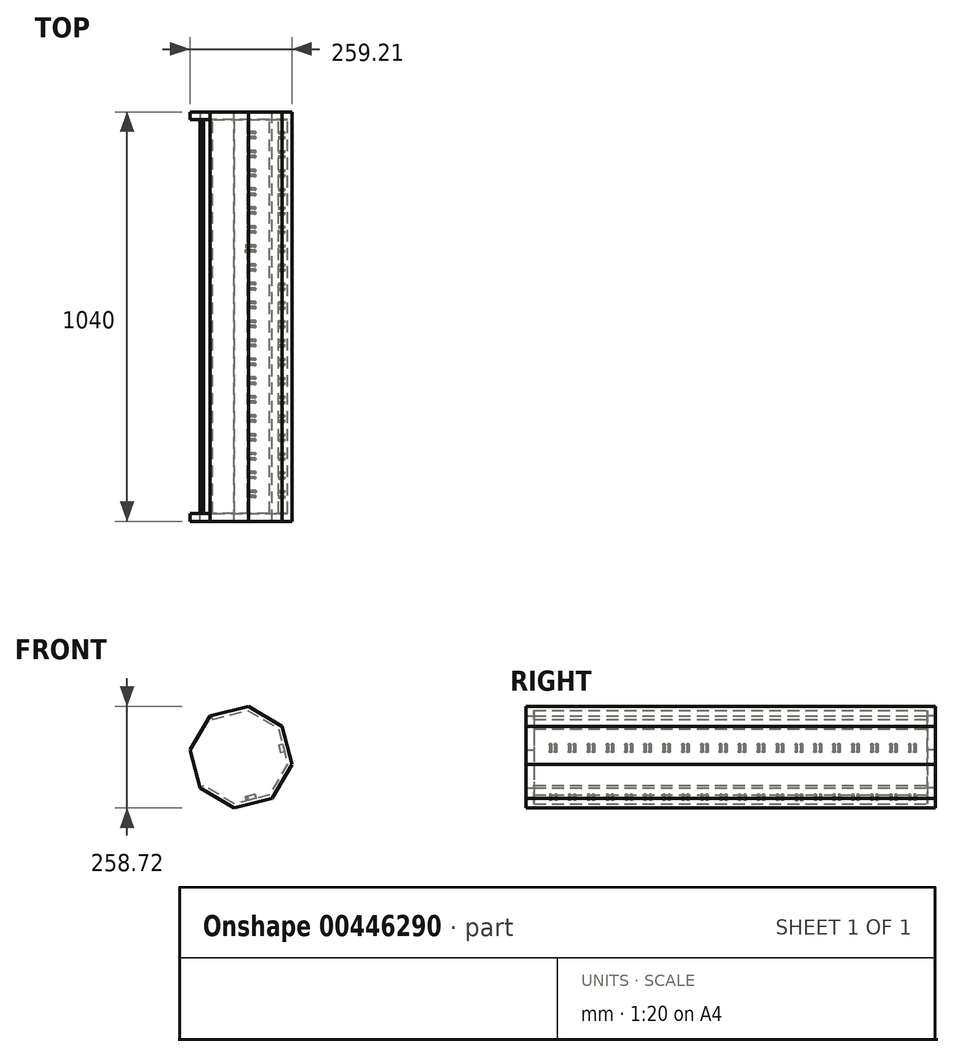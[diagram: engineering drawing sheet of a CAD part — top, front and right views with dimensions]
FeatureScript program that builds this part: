
annotation { "Feature Type Name" : "Feature", "Feature Type Description" : "" }
export const myFeature = defineFeature(function(context is Context, id is Id, definition is map)
    precondition{}
    {
        {
            var Q0;
            Q0=qCreatedBy(makeId("Front.planeOp"),FACE);
            var sketch = newSketch(context, id + "F0", { "sketchPlane" : qUnion([Q0])});
            skCircle(sketch, "E0.cCircle", {"center": v(-103.92, 114.28) * mm, "radius": 120.71 * mm, "construction": true});
            skLineSegment(sketch, "E0.0", {"start": v(25.44, 95.92) * mm, "end": v(-25.44, 9.82) * mm});
            skLineSegment(sketch, "E0.1", {"start": v(-25.44, 9.82) * mm, "end": v(-122.29, -15.08) * mm});
            skLineSegment(sketch, "E0.2", {"start": v(-122.29, -15.08) * mm, "end": v(-208.38, 35.8) * mm});
            skLineSegment(sketch, "E0.5", {"start": v(-182.4, 218.74) * mm, "end": v(-85.56, 243.64) * mm});
            skLineSegment(sketch, "E0.6", {"start": v(-85.56, 243.64) * mm, "end": v(0.53, 192.77) * mm});
            skLineSegment(sketch, "E0.7", {"start": v(0.53, 192.77) * mm, "end": v(25.44, 95.92) * mm});
            skPoint(sketch, "E0.0.midPoint", {"position": v(0, 52.87) * mm});
            skCircle(sketch, "E1.cCircle", {"center": v(-103.92, 114.28) * mm, "radius": 110.71 * mm, "construction": true});
            skLineSegment(sketch, "E1.0", {"start": v(-8.12, 186.26) * mm, "end": v(14.72, 97.44) * mm});
            skLineSegment(sketch, "E1.1", {"start": v(14.72, 97.44) * mm, "end": v(-31.94, 18.48) * mm});
            skLineSegment(sketch, "E1.2", {"start": v(-31.94, 18.48) * mm, "end": v(-120.77, -4.36) * mm});
            skLineSegment(sketch, "E1.3", {"start": v(-120.77, -4.36) * mm, "end": v(-199.73, 42.3) * mm});
            skLineSegment(sketch, "E1.6", {"start": v(-175.9, 210.08) * mm, "end": v(-87.08, 232.92) * mm});
            skLineSegment(sketch, "E1.7", {"start": v(-87.08, 232.92) * mm, "end": v(-8.12, 186.26) * mm});
            skPoint(sketch, "E1.0.midPoint", {"position": v(3.3, 141.85) * mm});
            skLineSegment(sketch, "E2", {"start": v(-182.4, 218.74) * mm, "end": v(-175.9, 210.08) * mm});
            skLineSegment(sketch, "E3", {"start": v(-208.38, 35.8) * mm, "end": v(-199.73, 42.3) * mm});
            skSolve(sketch);
        }
        {
            var Q0;
            Q0 = qSketchRegion(id + "F0", true);
            extrude(context, id + "F1", {"entities" : qUnion([Q0]), "depth" : 1000 * mm});
        }
        {
            var Q0;
            Q0=makeQuery(id+"F1.opExtrude","CAP_FACE",FACE,{"disambiguationData":[OSD([sQuery(id+"F0.wireOp",EDGE,"E0.0"),sQuery(id+"F0.wireOp",EDGE,"E0.1"),sQuery(id+"F0.wireOp",EDGE,"E0.2"),sQuery(id+"F0.wireOp",EDGE,"E0.5"),sQuery(id+"F0.wireOp",EDGE,"E0.6"),sQuery(id+"F0.wireOp",EDGE,"E0.7"),sQuery(id+"F0.wireOp",EDGE,"E1.0"),sQuery(id+"F0.wireOp",EDGE,"E1.1"),sQuery(id+"F0.wireOp",EDGE,"E1.2"),sQuery(id+"F0.wireOp",EDGE,"E1.3"),sQuery(id+"F0.wireOp",EDGE,"E1.6"),sQuery(id+"F0.wireOp",EDGE,"E1.7"),sQuery(id+"F0.wireOp",EDGE,"E2"),sQuery(id+"F0.wireOp",EDGE,"E3")])],"isStart":false});
            var sketch = newSketch(context, id + "F2", { "sketchPlane" : qUnion([Q0])});
            skLineSegment(sketch, "E4", {"start": v(-182.4, 218.74) * mm, "end": v(-233.28, 132.65) * mm});
            skLineSegment(sketch, "E5", {"start": v(-233.28, 132.65) * mm, "end": v(-208.38, 35.8) * mm});
            skLineSegment(sketch, "E6", {"start": v(-208.38, 35.8) * mm, "end": v(-122.29, -15.08) * mm});
            skLineSegment(sketch, "E7", {"start": v(-122.29, -15.08) * mm, "end": v(-25.44, 9.82) * mm});
            skLineSegment(sketch, "E8", {"start": v(-25.44, 9.82) * mm, "end": v(25.44, 95.92) * mm});
            skLineSegment(sketch, "E9", {"start": v(25.44, 95.92) * mm, "end": v(0.53, 192.77) * mm});
            skLineSegment(sketch, "E10", {"start": v(0.53, 192.77) * mm, "end": v(-85.56, 243.64) * mm});
            skLineSegment(sketch, "E11", {"start": v(-85.56, 243.64) * mm, "end": v(-182.4, 218.74) * mm});
            skSolve(sketch);
        }
        {
            var Q0;
            Q0 = qSketchRegion(id + "F2", true);
            extrude(context, id + "F3", {"entities" : qUnion([Q0]), "operationType" : NewBodyOperationType.ADD, "depth" : 20 * mm});
        }
        {
            var Q0;
            Q0=makeQuery(id+"F1.opExtrude","CAP_FACE",FACE,{"disambiguationData":[OSD([sQuery(id+"F0.wireOp",EDGE,"E0.0"),sQuery(id+"F0.wireOp",EDGE,"E0.1"),sQuery(id+"F0.wireOp",EDGE,"E0.2"),sQuery(id+"F0.wireOp",EDGE,"E0.5"),sQuery(id+"F0.wireOp",EDGE,"E0.6"),sQuery(id+"F0.wireOp",EDGE,"E0.7"),sQuery(id+"F0.wireOp",EDGE,"E1.0"),sQuery(id+"F0.wireOp",EDGE,"E1.1"),sQuery(id+"F0.wireOp",EDGE,"E1.2"),sQuery(id+"F0.wireOp",EDGE,"E1.3"),sQuery(id+"F0.wireOp",EDGE,"E1.6"),sQuery(id+"F0.wireOp",EDGE,"E1.7"),sQuery(id+"F0.wireOp",EDGE,"E2"),sQuery(id+"F0.wireOp",EDGE,"E3")])],"isStart":true});
            var sketch = newSketch(context, id + "F4", { "sketchPlane" : qUnion([Q0])});
            skLineSegment(sketch, "E12", {"start": v(182.4, 218.74) * mm, "end": v(85.56, 243.64) * mm});
            skLineSegment(sketch, "E13", {"start": v(85.56, 243.64) * mm, "end": v(-0.53, 192.77) * mm});
            skLineSegment(sketch, "E14", {"start": v(-0.53, 192.77) * mm, "end": v(-25.44, 95.92) * mm});
            skLineSegment(sketch, "E15", {"start": v(-25.44, 95.92) * mm, "end": v(25.44, 9.82) * mm});
            skLineSegment(sketch, "E16", {"start": v(25.44, 9.82) * mm, "end": v(122.29, -15.08) * mm});
            skLineSegment(sketch, "E17", {"start": v(122.29, -15.08) * mm, "end": v(208.38, 35.8) * mm});
            skLineSegment(sketch, "E18", {"start": v(208.38, 35.8) * mm, "end": v(233.77, 133.25) * mm});
            skLineSegment(sketch, "E19", {"start": v(233.77, 133.25) * mm, "end": v(182.4, 218.74) * mm});
            skSolve(sketch);
        }
        {
            var Q0;
            Q0 = qSketchRegion(id + "F4", true);
            extrude(context, id + "F5", {"entities" : qUnion([Q0]), "operationType" : NewBodyOperationType.ADD, "depth" : 20 * mm});
        }
        {
            var Q0;
            Q0=makeQuery(id+"F1.opExtrude","SWEPT_FACE",FACE,{"disambiguationData":[OSD([sQuery(id+"F0.wireOp",EDGE,"E1.0")])]});
            var sketch = newSketch(context, id + "F6", { "sketchPlane" : qUnion([Q0])});
            skLineSegment(sketch, "E20.bottom", {"start": v(30, 143.31) * mm, "end": v(35, 143.31) * mm});
            skLineSegment(sketch, "E20.top", {"start": v(30, 123.31) * mm, "end": v(35, 123.31) * mm});
            skLineSegment(sketch, "E20.left", {"start": v(30, 143.31) * mm, "end": v(30, 123.31) * mm});
            skLineSegment(sketch, "E20.right", {"start": v(35, 143.31) * mm, "end": v(35, 123.31) * mm});
            skLineSegment(sketch, "E21.bottom", {"start": v(43, 143.33) * mm, "end": v(48, 143.33) * mm});
            skLineSegment(sketch, "E21.top", {"start": v(43, 123.33) * mm, "end": v(48, 123.33) * mm});
            skLineSegment(sketch, "E21.left", {"start": v(43, 143.33) * mm, "end": v(43, 123.33) * mm});
            skLineSegment(sketch, "E21.right", {"start": v(48, 143.33) * mm, "end": v(48, 123.33) * mm});
            skLineSegment(sketch, "E22.bottom", {"start": v(78, 143.31) * mm, "end": v(83.3, 143.31) * mm});
            skLineSegment(sketch, "E22.top", {"start": v(78, 123.31) * mm, "end": v(83.3, 123.31) * mm});
            skLineSegment(sketch, "E22.left", {"start": v(78, 143.31) * mm, "end": v(78, 123.31) * mm});
            skLineSegment(sketch, "E22.right", {"start": v(83.3, 143.31) * mm, "end": v(83.3, 123.31) * mm});
            skLineSegment(sketch, "E23.bottom", {"start": v(91.3, 143.31) * mm, "end": v(96.3, 143.31) * mm});
            skLineSegment(sketch, "E23.top", {"start": v(91.3, 123.09) * mm, "end": v(96.3, 123.09) * mm});
            skLineSegment(sketch, "E23.left", {"start": v(91.3, 143.31) * mm, "end": v(91.3, 123.09) * mm});
            skLineSegment(sketch, "E23.right", {"start": v(96.3, 143.31) * mm, "end": v(96.3, 123.09) * mm});
            skLineSegment(sketch, "E24.bottom", {"start": v(126.3, 143.31) * mm, "end": v(131.3, 143.31) * mm});
            skLineSegment(sketch, "E24.top", {"start": v(126.3, 123.31) * mm, "end": v(131.3, 123.31) * mm});
            skLineSegment(sketch, "E24.left", {"start": v(126.3, 143.31) * mm, "end": v(126.3, 123.31) * mm});
            skLineSegment(sketch, "E24.right", {"start": v(131.3, 143.31) * mm, "end": v(131.3, 123.31) * mm});
            skLineSegment(sketch, "E25.bottom", {"start": v(139.3, 143.31) * mm, "end": v(144.3, 143.31) * mm});
            skLineSegment(sketch, "E25.top", {"start": v(139.3, 123.54) * mm, "end": v(144.3, 123.54) * mm});
            skLineSegment(sketch, "E25.left", {"start": v(139.3, 143.31) * mm, "end": v(139.3, 123.54) * mm});
            skLineSegment(sketch, "E25.right", {"start": v(144.3, 143.31) * mm, "end": v(144.3, 123.54) * mm});
            skLineSegment(sketch, "E26.bottom", {"start": v(174.3, 143.31) * mm, "end": v(179.3, 143.31) * mm});
            skLineSegment(sketch, "E26.top", {"start": v(174.3, 123.31) * mm, "end": v(179.3, 123.31) * mm});
            skLineSegment(sketch, "E26.left", {"start": v(174.3, 143.31) * mm, "end": v(174.3, 123.31) * mm});
            skLineSegment(sketch, "E26.right", {"start": v(179.3, 143.31) * mm, "end": v(179.3, 123.31) * mm});
            skLineSegment(sketch, "E27.bottom", {"start": v(187.3, 143.31) * mm, "end": v(192.3, 143.31) * mm});
            skLineSegment(sketch, "E27.top", {"start": v(187.3, 123.31) * mm, "end": v(192.3, 123.31) * mm});
            skLineSegment(sketch, "E27.left", {"start": v(187.3, 143.31) * mm, "end": v(187.3, 123.31) * mm});
            skLineSegment(sketch, "E27.right", {"start": v(192.3, 143.31) * mm, "end": v(192.3, 123.31) * mm});
            skLineSegment(sketch, "E28.bottom", {"start": v(222.3, 143.31) * mm, "end": v(227.3, 143.31) * mm});
            skLineSegment(sketch, "E28.top", {"start": v(222.3, 123.31) * mm, "end": v(227.3, 123.31) * mm});
            skLineSegment(sketch, "E28.left", {"start": v(222.3, 143.31) * mm, "end": v(222.3, 123.31) * mm});
            skLineSegment(sketch, "E28.right", {"start": v(227.3, 143.31) * mm, "end": v(227.3, 123.31) * mm});
            skLineSegment(sketch, "E29.bottom", {"start": v(235.3, 143.31) * mm, "end": v(240.3, 143.31) * mm});
            skLineSegment(sketch, "E29.top", {"start": v(235.3, 123.31) * mm, "end": v(240.3, 123.31) * mm});
            skLineSegment(sketch, "E29.left", {"start": v(235.3, 143.31) * mm, "end": v(235.3, 123.31) * mm});
            skLineSegment(sketch, "E29.right", {"start": v(240.3, 143.31) * mm, "end": v(240.3, 123.31) * mm});
            skLineSegment(sketch, "E30.bottom", {"start": v(270.3, 143.31) * mm, "end": v(275.3, 143.31) * mm});
            skLineSegment(sketch, "E30.top", {"start": v(270.3, 123.31) * mm, "end": v(275.3, 123.31) * mm});
            skLineSegment(sketch, "E30.left", {"start": v(270.3, 143.31) * mm, "end": v(270.3, 123.31) * mm});
            skLineSegment(sketch, "E30.right", {"start": v(275.3, 143.31) * mm, "end": v(275.3, 123.31) * mm});
            skLineSegment(sketch, "E31.bottom", {"start": v(283.3, 143.31) * mm, "end": v(288.3, 143.31) * mm});
            skLineSegment(sketch, "E31.top", {"start": v(283.3, 123.31) * mm, "end": v(288.3, 123.31) * mm});
            skLineSegment(sketch, "E31.left", {"start": v(283.3, 143.31) * mm, "end": v(283.3, 123.31) * mm});
            skLineSegment(sketch, "E31.right", {"start": v(288.3, 143.31) * mm, "end": v(288.3, 123.31) * mm});
            skLineSegment(sketch, "E32.bottom", {"start": v(318.3, 143.31) * mm, "end": v(323.3, 143.31) * mm});
            skLineSegment(sketch, "E32.top", {"start": v(318.3, 123.31) * mm, "end": v(323.3, 123.31) * mm});
            skLineSegment(sketch, "E32.left", {"start": v(318.3, 143.31) * mm, "end": v(318.3, 123.31) * mm});
            skLineSegment(sketch, "E32.right", {"start": v(323.3, 143.31) * mm, "end": v(323.3, 123.31) * mm});
            skLineSegment(sketch, "E33.bottom", {"start": v(331.3, 143.31) * mm, "end": v(336.3, 143.31) * mm});
            skLineSegment(sketch, "E33.top", {"start": v(331.3, 123.31) * mm, "end": v(336.3, 123.31) * mm});
            skLineSegment(sketch, "E33.left", {"start": v(331.3, 143.31) * mm, "end": v(331.3, 123.31) * mm});
            skLineSegment(sketch, "E33.right", {"start": v(336.3, 143.31) * mm, "end": v(336.3, 123.31) * mm});
            skLineSegment(sketch, "E34.bottom", {"start": v(366.3, 143.31) * mm, "end": v(371.3, 143.31) * mm});
            skLineSegment(sketch, "E34.top", {"start": v(366.3, 123.31) * mm, "end": v(371.3, 123.31) * mm});
            skLineSegment(sketch, "E34.left", {"start": v(366.3, 143.31) * mm, "end": v(366.3, 123.31) * mm});
            skLineSegment(sketch, "E34.right", {"start": v(371.3, 143.31) * mm, "end": v(371.3, 123.31) * mm});
            skPoint(sketch, "E35.firstSnap0", {"position": v(368.8, 143.31) * mm});
            skLineSegment(sketch, "E35.bottom", {"start": v(379.3, 143.31) * mm, "end": v(384.3, 143.31) * mm});
            skLineSegment(sketch, "E35.top", {"start": v(379.3, 123.31) * mm, "end": v(384.3, 123.31) * mm});
            skLineSegment(sketch, "E35.left", {"start": v(379.3, 143.31) * mm, "end": v(379.3, 123.31) * mm});
            skLineSegment(sketch, "E35.right", {"start": v(384.3, 143.31) * mm, "end": v(384.3, 123.31) * mm});
            skLineSegment(sketch, "E36.bottom", {"start": v(414.3, 143.31) * mm, "end": v(419.3, 143.31) * mm});
            skLineSegment(sketch, "E36.top", {"start": v(414.3, 123.31) * mm, "end": v(419.3, 123.31) * mm});
            skLineSegment(sketch, "E36.left", {"start": v(414.3, 143.31) * mm, "end": v(414.3, 123.31) * mm});
            skLineSegment(sketch, "E36.right", {"start": v(419.3, 143.31) * mm, "end": v(419.3, 123.31) * mm});
            skPoint(sketch, "E37.firstSnap0", {"position": v(416.8, 143.31) * mm});
            skLineSegment(sketch, "E37.bottom", {"start": v(427.3, 143.31) * mm, "end": v(432.3, 143.31) * mm});
            skLineSegment(sketch, "E37.top", {"start": v(427.3, 123.31) * mm, "end": v(432.3, 123.31) * mm});
            skLineSegment(sketch, "E37.left", {"start": v(427.3, 143.31) * mm, "end": v(427.3, 123.31) * mm});
            skLineSegment(sketch, "E37.right", {"start": v(432.3, 143.31) * mm, "end": v(432.3, 123.31) * mm});
            skLineSegment(sketch, "E38.bottom", {"start": v(462.3, 143.31) * mm, "end": v(467.3, 143.31) * mm});
            skLineSegment(sketch, "E38.top", {"start": v(462.3, 123.31) * mm, "end": v(467.3, 123.31) * mm});
            skLineSegment(sketch, "E38.left", {"start": v(462.3, 143.31) * mm, "end": v(462.3, 123.31) * mm});
            skLineSegment(sketch, "E38.right", {"start": v(467.3, 143.31) * mm, "end": v(467.3, 123.31) * mm});
            skLineSegment(sketch, "E39.bottom", {"start": v(475.3, 143.31) * mm, "end": v(480.3, 143.31) * mm});
            skLineSegment(sketch, "E39.top", {"start": v(475.3, 123.31) * mm, "end": v(480.3, 123.31) * mm});
            skLineSegment(sketch, "E39.left", {"start": v(475.3, 143.31) * mm, "end": v(475.3, 123.31) * mm});
            skLineSegment(sketch, "E39.right", {"start": v(480.3, 143.31) * mm, "end": v(480.3, 123.31) * mm});
            skLineSegment(sketch, "E40.bottom", {"start": v(510.3, 143.31) * mm, "end": v(515.3, 143.31) * mm});
            skLineSegment(sketch, "E40.top", {"start": v(510.3, 123.31) * mm, "end": v(515.3, 123.31) * mm});
            skLineSegment(sketch, "E40.left", {"start": v(510.3, 143.31) * mm, "end": v(510.3, 123.31) * mm});
            skLineSegment(sketch, "E40.right", {"start": v(515.3, 143.31) * mm, "end": v(515.3, 123.31) * mm});
            skPoint(sketch, "E41.firstSnap0", {"position": v(512.8, 143.31) * mm});
            skLineSegment(sketch, "E41.bottom", {"start": v(523.3, 143.31) * mm, "end": v(528.3, 143.31) * mm});
            skLineSegment(sketch, "E41.top", {"start": v(523.3, 123.31) * mm, "end": v(528.3, 123.31) * mm});
            skLineSegment(sketch, "E41.left", {"start": v(523.3, 143.31) * mm, "end": v(523.3, 123.31) * mm});
            skLineSegment(sketch, "E41.right", {"start": v(528.3, 143.31) * mm, "end": v(528.3, 123.31) * mm});
            skPoint(sketch, "E42.firstSnap0", {"position": v(525.8, 143.31) * mm});
            skLineSegment(sketch, "E42.bottom", {"start": v(558.3, 143.31) * mm, "end": v(563.3, 143.31) * mm});
            skLineSegment(sketch, "E42.top", {"start": v(558.3, 123.31) * mm, "end": v(563.3, 123.31) * mm});
            skLineSegment(sketch, "E42.left", {"start": v(558.3, 143.31) * mm, "end": v(558.3, 123.31) * mm});
            skLineSegment(sketch, "E42.right", {"start": v(563.3, 143.31) * mm, "end": v(563.3, 123.31) * mm});
            skPoint(sketch, "E43.firstSnap0", {"position": v(560.8, 143.31) * mm});
            skLineSegment(sketch, "E43.bottom", {"start": v(571.3, 143.31) * mm, "end": v(576.3, 143.31) * mm});
            skLineSegment(sketch, "E43.top", {"start": v(571.3, 123.31) * mm, "end": v(576.3, 123.31) * mm});
            skLineSegment(sketch, "E43.left", {"start": v(571.3, 143.31) * mm, "end": v(571.3, 123.31) * mm});
            skLineSegment(sketch, "E43.right", {"start": v(576.3, 143.31) * mm, "end": v(576.3, 123.31) * mm});
            skPoint(sketch, "E44.firstSnap0", {"position": v(573.8, 143.31) * mm});
            skLineSegment(sketch, "E44.bottom", {"start": v(606.3, 143.31) * mm, "end": v(611.3, 143.31) * mm});
            skLineSegment(sketch, "E44.top", {"start": v(606.3, 123.31) * mm, "end": v(611.3, 123.31) * mm});
            skLineSegment(sketch, "E44.left", {"start": v(606.3, 143.31) * mm, "end": v(606.3, 123.31) * mm});
            skLineSegment(sketch, "E44.right", {"start": v(611.3, 143.31) * mm, "end": v(611.3, 123.31) * mm});
            skPoint(sketch, "E45.firstSnap0", {"position": v(608.8, 143.31) * mm});
            skLineSegment(sketch, "E45.bottom", {"start": v(619.3, 143.31) * mm, "end": v(624.3, 143.31) * mm});
            skLineSegment(sketch, "E45.top", {"start": v(619.3, 123.31) * mm, "end": v(624.3, 123.31) * mm});
            skLineSegment(sketch, "E45.left", {"start": v(619.3, 143.31) * mm, "end": v(619.3, 123.31) * mm});
            skLineSegment(sketch, "E45.right", {"start": v(624.3, 143.31) * mm, "end": v(624.3, 123.31) * mm});
            skLineSegment(sketch, "E46.bottom", {"start": v(654.3, 143.31) * mm, "end": v(659.3, 143.31) * mm});
            skLineSegment(sketch, "E46.top", {"start": v(654.3, 123.31) * mm, "end": v(659.3, 123.31) * mm});
            skLineSegment(sketch, "E46.left", {"start": v(654.3, 143.31) * mm, "end": v(654.3, 123.31) * mm});
            skLineSegment(sketch, "E46.right", {"start": v(659.3, 143.31) * mm, "end": v(659.3, 123.31) * mm});
            skLineSegment(sketch, "E47.bottom", {"start": v(667.3, 143.31) * mm, "end": v(672.3, 143.31) * mm});
            skLineSegment(sketch, "E47.top", {"start": v(667.3, 123.31) * mm, "end": v(672.3, 123.31) * mm});
            skLineSegment(sketch, "E47.left", {"start": v(667.3, 143.31) * mm, "end": v(667.3, 123.31) * mm});
            skLineSegment(sketch, "E47.right", {"start": v(672.3, 143.31) * mm, "end": v(672.3, 123.31) * mm});
            skLineSegment(sketch, "E48.bottom", {"start": v(702.3, 143.31) * mm, "end": v(707.3, 143.31) * mm});
            skLineSegment(sketch, "E48.top", {"start": v(702.3, 123.31) * mm, "end": v(707.3, 123.31) * mm});
            skLineSegment(sketch, "E48.left", {"start": v(702.3, 143.31) * mm, "end": v(702.3, 123.31) * mm});
            skLineSegment(sketch, "E48.right", {"start": v(707.3, 143.31) * mm, "end": v(707.3, 123.31) * mm});
            skPoint(sketch, "E49.firstSnap0", {"position": v(704.8, 143.31) * mm});
            skLineSegment(sketch, "E49.bottom", {"start": v(715.3, 143.31) * mm, "end": v(720.3, 143.31) * mm});
            skLineSegment(sketch, "E49.top", {"start": v(715.3, 123.31) * mm, "end": v(720.3, 123.31) * mm});
            skLineSegment(sketch, "E49.left", {"start": v(715.3, 143.31) * mm, "end": v(715.3, 123.31) * mm});
            skLineSegment(sketch, "E49.right", {"start": v(720.3, 143.31) * mm, "end": v(720.3, 123.31) * mm});
            skPoint(sketch, "E50.firstSnap0", {"position": v(717.8, 143.31) * mm});
            skLineSegment(sketch, "E50.bottom", {"start": v(750.3, 143.31) * mm, "end": v(755.3, 143.31) * mm});
            skLineSegment(sketch, "E50.top", {"start": v(750.3, 123.31) * mm, "end": v(755.3, 123.31) * mm});
            skLineSegment(sketch, "E50.left", {"start": v(750.3, 143.31) * mm, "end": v(750.3, 123.31) * mm});
            skLineSegment(sketch, "E50.right", {"start": v(755.3, 143.31) * mm, "end": v(755.3, 123.31) * mm});
            skPoint(sketch, "E51.firstSnap0", {"position": v(752.8, 143.31) * mm});
            skLineSegment(sketch, "E51.bottom", {"start": v(763.3, 143.31) * mm, "end": v(768.3, 143.31) * mm});
            skLineSegment(sketch, "E51.top", {"start": v(763.3, 123.31) * mm, "end": v(768.3, 123.31) * mm});
            skLineSegment(sketch, "E51.left", {"start": v(763.3, 143.31) * mm, "end": v(763.3, 123.31) * mm});
            skLineSegment(sketch, "E51.right", {"start": v(768.3, 143.31) * mm, "end": v(768.3, 123.31) * mm});
            skPoint(sketch, "E52.firstSnap0", {"position": v(765.8, 143.31) * mm});
            skLineSegment(sketch, "E52.bottom", {"start": v(798.3, 143.31) * mm, "end": v(803.3, 143.31) * mm});
            skLineSegment(sketch, "E52.top", {"start": v(798.3, 123.31) * mm, "end": v(803.3, 123.31) * mm});
            skLineSegment(sketch, "E52.left", {"start": v(798.3, 143.31) * mm, "end": v(798.3, 123.31) * mm});
            skLineSegment(sketch, "E52.right", {"start": v(803.3, 143.31) * mm, "end": v(803.3, 123.31) * mm});
            skPoint(sketch, "E53.firstSnap0", {"position": v(800.8, 143.31) * mm});
            skLineSegment(sketch, "E53.bottom", {"start": v(811.3, 143.31) * mm, "end": v(816.3, 143.31) * mm});
            skLineSegment(sketch, "E53.top", {"start": v(811.3, 123.31) * mm, "end": v(816.3, 123.31) * mm});
            skLineSegment(sketch, "E53.left", {"start": v(811.3, 143.31) * mm, "end": v(811.3, 123.31) * mm});
            skLineSegment(sketch, "E53.right", {"start": v(816.3, 143.31) * mm, "end": v(816.3, 123.31) * mm});
            skLineSegment(sketch, "E54.bottom", {"start": v(846.3, 143.31) * mm, "end": v(851.3, 143.31) * mm});
            skLineSegment(sketch, "E54.top", {"start": v(846.3, 123.31) * mm, "end": v(851.3, 123.31) * mm});
            skLineSegment(sketch, "E54.left", {"start": v(846.3, 143.31) * mm, "end": v(846.3, 123.31) * mm});
            skLineSegment(sketch, "E54.right", {"start": v(851.3, 143.31) * mm, "end": v(851.3, 123.31) * mm});
            skLineSegment(sketch, "E55.bottom", {"start": v(859.3, 143.31) * mm, "end": v(864.3, 143.31) * mm});
            skLineSegment(sketch, "E55.top", {"start": v(859.3, 123.31) * mm, "end": v(864.3, 123.31) * mm});
            skLineSegment(sketch, "E55.left", {"start": v(859.3, 143.31) * mm, "end": v(859.3, 123.31) * mm});
            skLineSegment(sketch, "E55.right", {"start": v(864.3, 143.31) * mm, "end": v(864.3, 123.31) * mm});
            skLineSegment(sketch, "E56.bottom", {"start": v(894.3, 143.31) * mm, "end": v(899.3, 143.31) * mm});
            skLineSegment(sketch, "E56.top", {"start": v(894.3, 123.3) * mm, "end": v(899.3, 123.3) * mm});
            skLineSegment(sketch, "E56.left", {"start": v(894.3, 143.31) * mm, "end": v(894.3, 123.3) * mm});
            skLineSegment(sketch, "E56.right", {"start": v(899.3, 143.31) * mm, "end": v(899.3, 123.3) * mm});
            skLineSegment(sketch, "E57.bottom", {"start": v(907.3, 143.31) * mm, "end": v(912.3, 143.31) * mm});
            skLineSegment(sketch, "E57.top", {"start": v(907.3, 123.31) * mm, "end": v(912.3, 123.31) * mm});
            skLineSegment(sketch, "E57.left", {"start": v(907.3, 143.31) * mm, "end": v(907.3, 123.31) * mm});
            skLineSegment(sketch, "E57.right", {"start": v(912.3, 143.31) * mm, "end": v(912.3, 123.31) * mm});
            skLineSegment(sketch, "E58.bottom", {"start": v(942.3, 143.31) * mm, "end": v(947.3, 143.31) * mm});
            skLineSegment(sketch, "E58.top", {"start": v(942.3, 123.31) * mm, "end": v(947.3, 123.31) * mm});
            skLineSegment(sketch, "E58.left", {"start": v(942.3, 143.31) * mm, "end": v(942.3, 123.31) * mm});
            skLineSegment(sketch, "E58.right", {"start": v(947.3, 143.31) * mm, "end": v(947.3, 123.31) * mm});
            skLineSegment(sketch, "E59.bottom", {"start": v(955.3, 143.31) * mm, "end": v(960.3, 143.31) * mm});
            skLineSegment(sketch, "E59.top", {"start": v(955.3, 123.31) * mm, "end": v(960.3, 123.31) * mm});
            skLineSegment(sketch, "E59.left", {"start": v(955.3, 143.31) * mm, "end": v(955.3, 123.31) * mm});
            skLineSegment(sketch, "E59.right", {"start": v(960.3, 143.31) * mm, "end": v(960.3, 123.31) * mm});
            skSolve(sketch);
        }
        {
            var Q0;
            Q0 = qSketchRegion(id + "F6", true);
            extrude(context, id + "F7", {"entities" : qUnion([Q0]), "operationType" : NewBodyOperationType.ADD, "depth" : 10 * mm});
        }
        {
            var Q0;
            Q0=makeQuery(id+"F1.opExtrude","SWEPT_FACE",FACE,{"disambiguationData":[OSD([sQuery(id+"F0.wireOp",EDGE,"E1.2")])]});
            var sketch = newSketch(context, id + "F8", { "sketchPlane" : qUnion([Q0])});
            skLineSegment(sketch, "E60.bottom", {"start": v(-62.18, -30) * mm, "end": v(-82.18, -30) * mm});
            skLineSegment(sketch, "E60.top", {"start": v(-62.18, -35) * mm, "end": v(-82.18, -35) * mm});
            skLineSegment(sketch, "E60.left", {"start": v(-62.18, -30) * mm, "end": v(-62.18, -35) * mm});
            skLineSegment(sketch, "E60.right", {"start": v(-82.18, -30) * mm, "end": v(-82.18, -35) * mm});
            skLineSegment(sketch, "E61.bottom", {"start": v(-62.18, -43) * mm, "end": v(-82.18, -43) * mm});
            skLineSegment(sketch, "E61.top", {"start": v(-62.18, -48) * mm, "end": v(-82.18, -48) * mm});
            skLineSegment(sketch, "E61.left", {"start": v(-62.18, -43) * mm, "end": v(-62.18, -48) * mm});
            skLineSegment(sketch, "E61.right", {"start": v(-82.18, -43) * mm, "end": v(-82.18, -48) * mm});
            skLineSegment(sketch, "E62.bottom", {"start": v(-62.18, -78) * mm, "end": v(-82.18, -78) * mm});
            skLineSegment(sketch, "E62.top", {"start": v(-62.18, -83) * mm, "end": v(-82.18, -83) * mm});
            skLineSegment(sketch, "E62.left", {"start": v(-62.18, -78) * mm, "end": v(-62.18, -83) * mm});
            skLineSegment(sketch, "E62.right", {"start": v(-82.18, -78) * mm, "end": v(-82.18, -83) * mm});
            skLineSegment(sketch, "E63.bottom", {"start": v(-62.18, -91) * mm, "end": v(-82.18, -91) * mm});
            skLineSegment(sketch, "E63.top", {"start": v(-62.18, -96) * mm, "end": v(-82.18, -96) * mm});
            skLineSegment(sketch, "E63.left", {"start": v(-62.18, -91) * mm, "end": v(-62.18, -96) * mm});
            skLineSegment(sketch, "E63.right", {"start": v(-82.18, -91) * mm, "end": v(-82.18, -96) * mm});
            skLineSegment(sketch, "E64.bottom", {"start": v(-62.18, -126) * mm, "end": v(-82.18, -126) * mm});
            skLineSegment(sketch, "E64.top", {"start": v(-62.18, -131) * mm, "end": v(-82.18, -131) * mm});
            skLineSegment(sketch, "E64.left", {"start": v(-62.18, -126) * mm, "end": v(-62.18, -131) * mm});
            skLineSegment(sketch, "E64.right", {"start": v(-82.18, -126) * mm, "end": v(-82.18, -131) * mm});
            skLineSegment(sketch, "E65.bottom", {"start": v(-62.18, -139) * mm, "end": v(-82.18, -139) * mm});
            skLineSegment(sketch, "E65.top", {"start": v(-62.18, -144) * mm, "end": v(-82.18, -144) * mm});
            skLineSegment(sketch, "E65.left", {"start": v(-62.18, -139) * mm, "end": v(-62.18, -144) * mm});
            skLineSegment(sketch, "E65.right", {"start": v(-82.18, -139) * mm, "end": v(-82.18, -144) * mm});
            skLineSegment(sketch, "E66.bottom", {"start": v(-62.18, -174) * mm, "end": v(-82.18, -174) * mm});
            skLineSegment(sketch, "E66.top", {"start": v(-62.18, -179) * mm, "end": v(-82.18, -179) * mm});
            skLineSegment(sketch, "E66.left", {"start": v(-62.18, -174) * mm, "end": v(-62.18, -179) * mm});
            skLineSegment(sketch, "E66.right", {"start": v(-82.18, -174) * mm, "end": v(-82.18, -179) * mm});
            skLineSegment(sketch, "E67.bottom", {"start": v(-62.18, -187) * mm, "end": v(-82.18, -187) * mm});
            skLineSegment(sketch, "E67.top", {"start": v(-62.18, -192) * mm, "end": v(-82.18, -192) * mm});
            skLineSegment(sketch, "E67.left", {"start": v(-62.18, -187) * mm, "end": v(-62.18, -192) * mm});
            skLineSegment(sketch, "E67.right", {"start": v(-82.18, -187) * mm, "end": v(-82.18, -192) * mm});
            skLineSegment(sketch, "E68.bottom", {"start": v(-62.18, -222) * mm, "end": v(-82.18, -222) * mm});
            skLineSegment(sketch, "E68.top", {"start": v(-62.18, -227) * mm, "end": v(-82.18, -227) * mm});
            skLineSegment(sketch, "E68.left", {"start": v(-62.18, -222) * mm, "end": v(-62.18, -227) * mm});
            skLineSegment(sketch, "E68.right", {"start": v(-82.18, -222) * mm, "end": v(-82.18, -227) * mm});
            skLineSegment(sketch, "E69.bottom", {"start": v(-62.18, -235) * mm, "end": v(-82.18, -235) * mm});
            skLineSegment(sketch, "E69.top", {"start": v(-62.18, -240) * mm, "end": v(-82.18, -240) * mm});
            skLineSegment(sketch, "E69.left", {"start": v(-62.18, -235) * mm, "end": v(-62.18, -240) * mm});
            skLineSegment(sketch, "E69.right", {"start": v(-82.18, -235) * mm, "end": v(-82.18, -240) * mm});
            skLineSegment(sketch, "E70.bottom", {"start": v(-62.18, -270) * mm, "end": v(-82.18, -270) * mm});
            skLineSegment(sketch, "E70.top", {"start": v(-62.18, -275) * mm, "end": v(-82.18, -275) * mm});
            skLineSegment(sketch, "E70.left", {"start": v(-62.18, -270) * mm, "end": v(-62.18, -275) * mm});
            skLineSegment(sketch, "E70.right", {"start": v(-82.18, -270) * mm, "end": v(-82.18, -275) * mm});
            skLineSegment(sketch, "E71.bottom", {"start": v(-62.18, -283) * mm, "end": v(-82.18, -283) * mm});
            skLineSegment(sketch, "E71.top", {"start": v(-62.18, -288) * mm, "end": v(-82.18, -288) * mm});
            skLineSegment(sketch, "E71.left", {"start": v(-62.18, -283) * mm, "end": v(-62.18, -288) * mm});
            skLineSegment(sketch, "E71.right", {"start": v(-82.18, -283) * mm, "end": v(-82.18, -288) * mm});
            skLineSegment(sketch, "E72.bottom", {"start": v(-62.18, -318) * mm, "end": v(-86.54, -318) * mm});
            skLineSegment(sketch, "E72.top", {"start": v(-62.18, -323) * mm, "end": v(-86.54, -323) * mm});
            skLineSegment(sketch, "E72.left", {"start": v(-62.18, -318) * mm, "end": v(-62.18, -323) * mm});
            skLineSegment(sketch, "E72.right", {"start": v(-86.54, -318) * mm, "end": v(-86.54, -323) * mm});
            skLineSegment(sketch, "E73.bottom", {"start": v(-62.18, -331) * mm, "end": v(-86.93, -331) * mm});
            skLineSegment(sketch, "E73.top", {"start": v(-62.18, -336) * mm, "end": v(-86.93, -336) * mm});
            skLineSegment(sketch, "E73.left", {"start": v(-62.18, -331) * mm, "end": v(-62.18, -336) * mm});
            skLineSegment(sketch, "E73.right", {"start": v(-86.93, -331) * mm, "end": v(-86.93, -336) * mm});
            skLineSegment(sketch, "E74.bottom", {"start": v(-62.18, -366) * mm, "end": v(-82.18, -366) * mm});
            skLineSegment(sketch, "E74.top", {"start": v(-62.18, -371) * mm, "end": v(-82.18, -371) * mm});
            skLineSegment(sketch, "E74.left", {"start": v(-62.18, -366) * mm, "end": v(-62.18, -371) * mm});
            skLineSegment(sketch, "E74.right", {"start": v(-82.18, -366) * mm, "end": v(-82.18, -371) * mm});
            skLineSegment(sketch, "E75.bottom", {"start": v(-62.18, -379) * mm, "end": v(-82.18, -379) * mm});
            skLineSegment(sketch, "E75.top", {"start": v(-62.18, -384) * mm, "end": v(-82.18, -384) * mm});
            skLineSegment(sketch, "E75.left", {"start": v(-62.18, -379) * mm, "end": v(-62.18, -384) * mm});
            skLineSegment(sketch, "E75.right", {"start": v(-82.18, -379) * mm, "end": v(-82.18, -384) * mm});
            skLineSegment(sketch, "E76.bottom", {"start": v(-62.18, -414) * mm, "end": v(-82.18, -414) * mm});
            skLineSegment(sketch, "E76.top", {"start": v(-62.18, -419) * mm, "end": v(-82.18, -419) * mm});
            skLineSegment(sketch, "E76.left", {"start": v(-62.18, -414) * mm, "end": v(-62.18, -419) * mm});
            skLineSegment(sketch, "E76.right", {"start": v(-82.18, -414) * mm, "end": v(-82.18, -419) * mm});
            skLineSegment(sketch, "E77.bottom", {"start": v(-62.18, -427) * mm, "end": v(-82.18, -427) * mm});
            skLineSegment(sketch, "E77.top", {"start": v(-62.18, -432) * mm, "end": v(-82.18, -432) * mm});
            skLineSegment(sketch, "E77.left", {"start": v(-62.18, -427) * mm, "end": v(-62.18, -432) * mm});
            skLineSegment(sketch, "E77.right", {"start": v(-82.18, -427) * mm, "end": v(-82.18, -432) * mm});
            skLineSegment(sketch, "E78.bottom", {"start": v(-62.18, -462) * mm, "end": v(-82.18, -462) * mm});
            skLineSegment(sketch, "E78.top", {"start": v(-62.18, -467) * mm, "end": v(-82.18, -467) * mm});
            skLineSegment(sketch, "E78.left", {"start": v(-62.18, -462) * mm, "end": v(-62.18, -467) * mm});
            skLineSegment(sketch, "E78.right", {"start": v(-82.18, -462) * mm, "end": v(-82.18, -467) * mm});
            skLineSegment(sketch, "E79.bottom", {"start": v(-62.18, -475) * mm, "end": v(-82.18, -475) * mm});
            skLineSegment(sketch, "E79.top", {"start": v(-62.18, -480) * mm, "end": v(-82.18, -480) * mm});
            skLineSegment(sketch, "E79.left", {"start": v(-62.18, -475) * mm, "end": v(-62.18, -480) * mm});
            skLineSegment(sketch, "E79.right", {"start": v(-82.18, -475) * mm, "end": v(-82.18, -480) * mm});
            skLineSegment(sketch, "E80.bottom", {"start": v(-62.18, -510) * mm, "end": v(-82.18, -510) * mm});
            skLineSegment(sketch, "E80.top", {"start": v(-62.18, -515) * mm, "end": v(-82.18, -515) * mm});
            skLineSegment(sketch, "E80.left", {"start": v(-62.18, -510) * mm, "end": v(-62.18, -515) * mm});
            skLineSegment(sketch, "E80.right", {"start": v(-82.18, -510) * mm, "end": v(-82.18, -515) * mm});
            skLineSegment(sketch, "E81.bottom", {"start": v(-62.18, -523) * mm, "end": v(-82.18, -523) * mm});
            skLineSegment(sketch, "E81.top", {"start": v(-62.18, -528) * mm, "end": v(-82.18, -528) * mm});
            skLineSegment(sketch, "E81.left", {"start": v(-62.18, -523) * mm, "end": v(-62.18, -528) * mm});
            skLineSegment(sketch, "E81.right", {"start": v(-82.18, -523) * mm, "end": v(-82.18, -528) * mm});
            skLineSegment(sketch, "E82.bottom", {"start": v(-62.18, -558) * mm, "end": v(-82.18, -558) * mm});
            skLineSegment(sketch, "E82.top", {"start": v(-62.18, -563) * mm, "end": v(-82.18, -563) * mm});
            skLineSegment(sketch, "E82.left", {"start": v(-62.18, -558) * mm, "end": v(-62.18, -563) * mm});
            skLineSegment(sketch, "E82.right", {"start": v(-82.18, -558) * mm, "end": v(-82.18, -563) * mm});
            skLineSegment(sketch, "E83.bottom", {"start": v(-62.18, -571) * mm, "end": v(-82.18, -571) * mm});
            skLineSegment(sketch, "E83.top", {"start": v(-62.18, -576) * mm, "end": v(-82.18, -576) * mm});
            skLineSegment(sketch, "E83.left", {"start": v(-62.18, -571) * mm, "end": v(-62.18, -576) * mm});
            skLineSegment(sketch, "E83.right", {"start": v(-82.18, -571) * mm, "end": v(-82.18, -576) * mm});
            skLineSegment(sketch, "E84.bottom", {"start": v(-62.18, -606) * mm, "end": v(-82.18, -606) * mm});
            skLineSegment(sketch, "E84.top", {"start": v(-62.18, -611) * mm, "end": v(-82.18, -611) * mm});
            skLineSegment(sketch, "E84.left", {"start": v(-62.18, -606) * mm, "end": v(-62.18, -611) * mm});
            skLineSegment(sketch, "E84.right", {"start": v(-82.18, -606) * mm, "end": v(-82.18, -611) * mm});
            skLineSegment(sketch, "E85.bottom", {"start": v(-62.18, -619) * mm, "end": v(-82.18, -619) * mm});
            skLineSegment(sketch, "E85.top", {"start": v(-62.18, -624) * mm, "end": v(-82.18, -624) * mm});
            skLineSegment(sketch, "E85.left", {"start": v(-62.18, -619) * mm, "end": v(-62.18, -624) * mm});
            skLineSegment(sketch, "E85.right", {"start": v(-82.18, -619) * mm, "end": v(-82.18, -624) * mm});
            skLineSegment(sketch, "E86.bottom", {"start": v(-62.18, -654) * mm, "end": v(-82.18, -654) * mm});
            skLineSegment(sketch, "E86.top", {"start": v(-62.18, -659) * mm, "end": v(-82.18, -659) * mm});
            skLineSegment(sketch, "E86.left", {"start": v(-62.18, -654) * mm, "end": v(-62.18, -659) * mm});
            skLineSegment(sketch, "E86.right", {"start": v(-82.18, -654) * mm, "end": v(-82.18, -659) * mm});
            skLineSegment(sketch, "E87.bottom", {"start": v(-62.18, -667) * mm, "end": v(-82.18, -667) * mm});
            skLineSegment(sketch, "E87.top", {"start": v(-62.18, -672) * mm, "end": v(-82.18, -672) * mm});
            skLineSegment(sketch, "E87.left", {"start": v(-62.18, -667) * mm, "end": v(-62.18, -672) * mm});
            skLineSegment(sketch, "E87.right", {"start": v(-82.18, -667) * mm, "end": v(-82.18, -672) * mm});
            skLineSegment(sketch, "E88.bottom", {"start": v(-62.18, -702) * mm, "end": v(-82.18, -702) * mm});
            skLineSegment(sketch, "E88.top", {"start": v(-62.18, -707) * mm, "end": v(-82.18, -707) * mm});
            skLineSegment(sketch, "E88.left", {"start": v(-62.18, -702) * mm, "end": v(-62.18, -707) * mm});
            skLineSegment(sketch, "E88.right", {"start": v(-82.18, -702) * mm, "end": v(-82.18, -707) * mm});
            skLineSegment(sketch, "E89.bottom", {"start": v(-62.18, -715) * mm, "end": v(-82.18, -715) * mm});
            skLineSegment(sketch, "E89.top", {"start": v(-62.18, -720) * mm, "end": v(-82.18, -720) * mm});
            skLineSegment(sketch, "E89.left", {"start": v(-62.18, -715) * mm, "end": v(-62.18, -720) * mm});
            skLineSegment(sketch, "E89.right", {"start": v(-82.18, -715) * mm, "end": v(-82.18, -720) * mm});
            skLineSegment(sketch, "E90.bottom", {"start": v(-62.18, -750) * mm, "end": v(-82.18, -750) * mm});
            skLineSegment(sketch, "E90.top", {"start": v(-62.18, -755) * mm, "end": v(-82.18, -755) * mm});
            skLineSegment(sketch, "E90.left", {"start": v(-62.18, -750) * mm, "end": v(-62.18, -755) * mm});
            skLineSegment(sketch, "E90.right", {"start": v(-82.18, -750) * mm, "end": v(-82.18, -755) * mm});
            skLineSegment(sketch, "E91.bottom", {"start": v(-62.18, -763) * mm, "end": v(-82.18, -763) * mm});
            skLineSegment(sketch, "E91.top", {"start": v(-62.18, -768) * mm, "end": v(-82.18, -768) * mm});
            skLineSegment(sketch, "E91.left", {"start": v(-62.18, -763) * mm, "end": v(-62.18, -768) * mm});
            skLineSegment(sketch, "E91.right", {"start": v(-82.18, -763) * mm, "end": v(-82.18, -768) * mm});
            skLineSegment(sketch, "E92.bottom", {"start": v(-62.18, -798) * mm, "end": v(-82.18, -798) * mm});
            skLineSegment(sketch, "E92.top", {"start": v(-62.18, -803) * mm, "end": v(-82.18, -803) * mm});
            skLineSegment(sketch, "E92.left", {"start": v(-62.18, -798) * mm, "end": v(-62.18, -803) * mm});
            skLineSegment(sketch, "E92.right", {"start": v(-82.18, -798) * mm, "end": v(-82.18, -803) * mm});
            skLineSegment(sketch, "E93.bottom", {"start": v(-62.18, -811) * mm, "end": v(-82.18, -811) * mm});
            skLineSegment(sketch, "E93.top", {"start": v(-62.18, -816) * mm, "end": v(-82.18, -816) * mm});
            skLineSegment(sketch, "E93.left", {"start": v(-62.18, -811) * mm, "end": v(-62.18, -816) * mm});
            skLineSegment(sketch, "E93.right", {"start": v(-82.18, -811) * mm, "end": v(-82.18, -816) * mm});
            skLineSegment(sketch, "E94.bottom", {"start": v(-62.18, -846) * mm, "end": v(-82.18, -846) * mm});
            skLineSegment(sketch, "E94.top", {"start": v(-62.18, -851) * mm, "end": v(-82.18, -851) * mm});
            skLineSegment(sketch, "E94.left", {"start": v(-62.18, -846) * mm, "end": v(-62.18, -851) * mm});
            skLineSegment(sketch, "E94.right", {"start": v(-82.18, -846) * mm, "end": v(-82.18, -851) * mm});
            skLineSegment(sketch, "E95.bottom", {"start": v(-62.18, -859) * mm, "end": v(-82.18, -859) * mm});
            skLineSegment(sketch, "E95.top", {"start": v(-62.18, -864) * mm, "end": v(-82.18, -864) * mm});
            skLineSegment(sketch, "E95.left", {"start": v(-62.18, -859) * mm, "end": v(-62.18, -864) * mm});
            skLineSegment(sketch, "E95.right", {"start": v(-82.18, -859) * mm, "end": v(-82.18, -864) * mm});
            skLineSegment(sketch, "E96.bottom", {"start": v(-62.18, -894) * mm, "end": v(-82.18, -894) * mm});
            skLineSegment(sketch, "E96.top", {"start": v(-62.18, -899) * mm, "end": v(-82.18, -899) * mm});
            skLineSegment(sketch, "E96.left", {"start": v(-62.18, -894) * mm, "end": v(-62.18, -899) * mm});
            skLineSegment(sketch, "E96.right", {"start": v(-82.18, -894) * mm, "end": v(-82.18, -899) * mm});
            skLineSegment(sketch, "E97.bottom", {"start": v(-62.18, -907) * mm, "end": v(-82.18, -907) * mm});
            skLineSegment(sketch, "E97.top", {"start": v(-62.18, -912) * mm, "end": v(-82.18, -912) * mm});
            skLineSegment(sketch, "E97.left", {"start": v(-62.18, -907) * mm, "end": v(-62.18, -912) * mm});
            skLineSegment(sketch, "E97.right", {"start": v(-82.18, -907) * mm, "end": v(-82.18, -912) * mm});
            skLineSegment(sketch, "E98.bottom", {"start": v(-61.65, -942) * mm, "end": v(-81.65, -942) * mm});
            skLineSegment(sketch, "E98.top", {"start": v(-61.65, -947) * mm, "end": v(-81.65, -947) * mm});
            skLineSegment(sketch, "E98.left", {"start": v(-61.65, -942) * mm, "end": v(-61.65, -947) * mm});
            skLineSegment(sketch, "E98.right", {"start": v(-81.65, -942) * mm, "end": v(-81.65, -947) * mm});
            skLineSegment(sketch, "E99.bottom", {"start": v(-62.18, -955) * mm, "end": v(-82.18, -955) * mm});
            skLineSegment(sketch, "E99.top", {"start": v(-62.18, -960) * mm, "end": v(-82.18, -960) * mm});
            skLineSegment(sketch, "E99.left", {"start": v(-62.18, -955) * mm, "end": v(-62.18, -960) * mm});
            skLineSegment(sketch, "E99.right", {"start": v(-82.18, -955) * mm, "end": v(-82.18, -960) * mm});
            skSolve(sketch);
        }
        {
            var Q0;
            Q0 = qSketchRegion(id + "F8", true);
            extrude(context, id + "F9", {"entities" : qUnion([Q0]), "operationType" : NewBodyOperationType.ADD, "depth" : 10 * mm});
        }
    });
